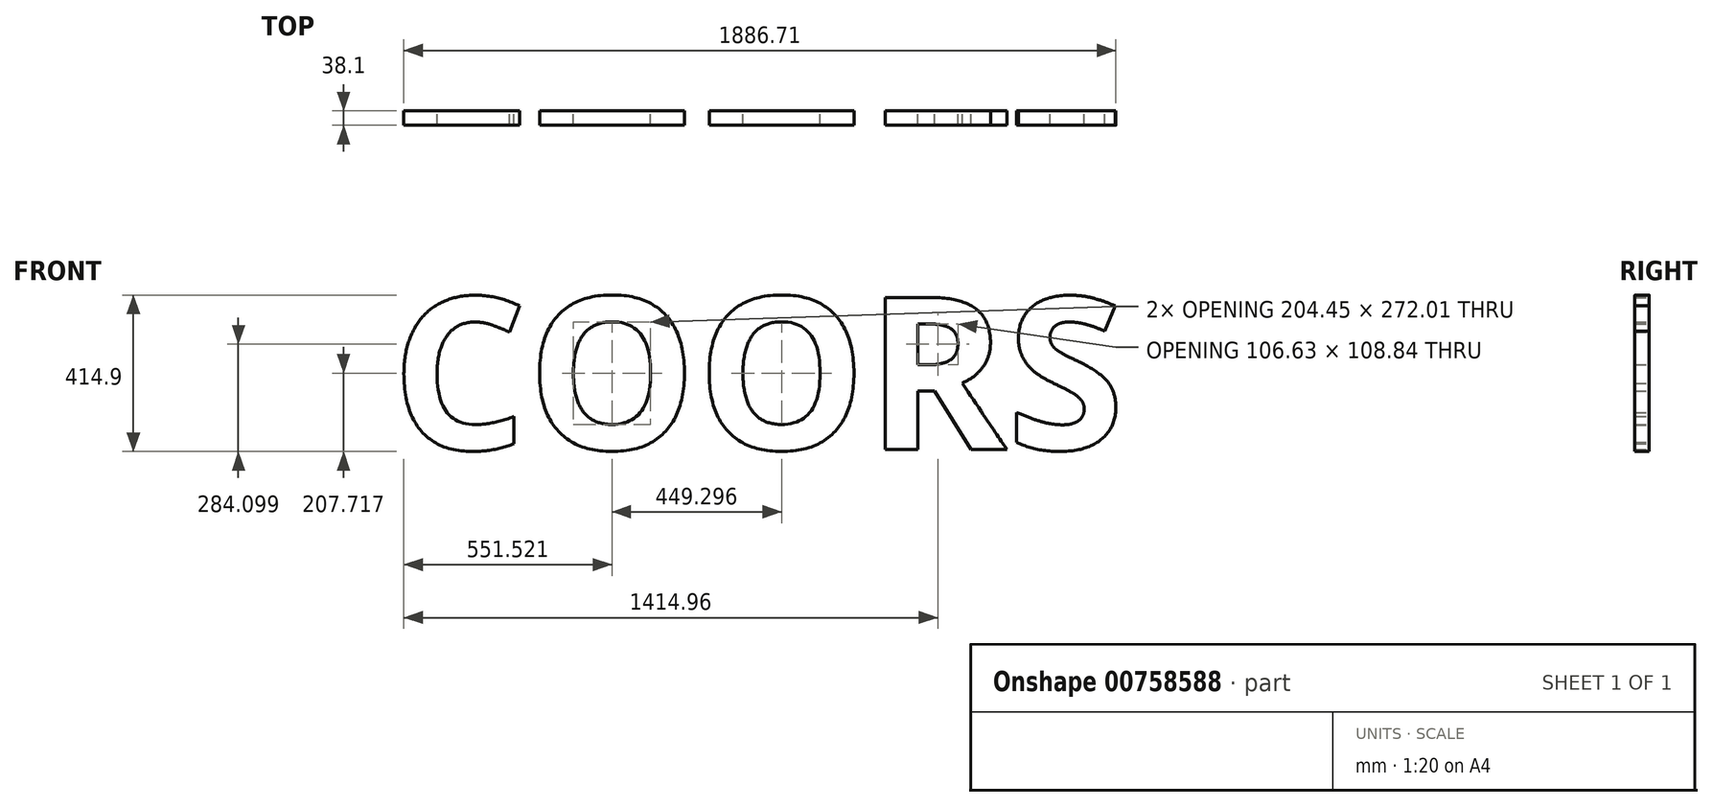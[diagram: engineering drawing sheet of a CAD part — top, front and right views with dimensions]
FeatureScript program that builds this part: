
annotation { "Feature Type Name" : "Feature", "Feature Type Description" : "" }
export const myFeature = defineFeature(function(context is Context, id is Id, definition is map)
    precondition{}
    {
        {
            var Q0;
            Q0=qCreatedBy(makeId("Front.planeOp"),FACE);
            var sketch = newSketch(context, id + "F0", { "sketchPlane" : qUnion([Q0])});
            skLineSegment(sketch, "E0.bottom", {"start": v(-1016, 228.6) * mm, "end": v(1016, 228.6) * mm});
            skLineSegment(sketch, "E0.top", {"start": v(-1016, -228.6) * mm, "end": v(1016, -228.6) * mm});
            skLineSegment(sketch, "E0.left", {"start": v(-1016, 228.6) * mm, "end": v(-1016, -228.6) * mm});
            skLineSegment(sketch, "E0.right", {"start": v(1016, 228.6) * mm, "end": v(1016, -228.6) * mm});
            skPoint(sketch, "E0.middle", {"position": v(0, 0) * mm});
            skText(sketch, "E1", { "text": "COORS", "fontName": "OpenSans-Bold.ttf"});
            const initialGuessF0  = {"E1": [-0.98102, -0.20588, 1, 0, 0.40643]};
            skSetInitialGuess(sketch, initialGuessF0);
            skSolve(sketch);
        }
        {
            var Q0;
            Q0=makeQuery(id+"F0.imprint","IMPRINT",FACE,{"disambiguationData":[TD([[makeQuery(id+"F0.imprint","IMPRINT",EDGE,{"derivedFrom":sQuery(id+"F0.wireOp",EDGE,"E1.sketch_text.stroke-0")}),-1.0]])]});
            extrude(context, id + "F1", {"entities" : qUnion([Q0]), "depth" : 38.1 * mm, "offsetDistance" : 25.4 * mm});
        }
        {
            var Q0;
            Q0=makeQuery(id+"F0.imprint","IMPRINT",FACE,{"disambiguationData":[TD([[makeQuery(id+"F0.imprint","IMPRINT",EDGE,{"derivedFrom":sQuery(id+"F0.wireOp",EDGE,"E1.sketch_text.stroke-15")}),-1.0]])]});
            extrude(context, id + "F2", {"entities" : qUnion([Q0]), "depth" : 38.1 * mm, "offsetDistance" : 25.4 * mm});
        }
        {
            var Q0;
            Q0=makeQuery(id+"F0.imprint","IMPRINT",FACE,{"disambiguationData":[TD([[makeQuery(id+"F0.imprint","IMPRINT",EDGE,{"derivedFrom":sQuery(id+"F0.wireOp",EDGE,"E1.sketch_text.stroke-29")}),-1.0]])]});
            var Q1;
            Q1=makeQuery(id+"F0.imprint","IMPRINT",FACE,{"disambiguationData":[TD([[makeQuery(id+"F0.imprint","IMPRINT",EDGE,{"derivedFrom":sQuery(id+"F0.wireOp",EDGE,"E1.sketch_text.stroke-43")}),-1.0]])]});
            var Q2;
            Q2=makeQuery(id+"F0.imprint","IMPRINT",FACE,{"disambiguationData":[TD([[makeQuery(id+"F0.imprint","IMPRINT",EDGE,{"derivedFrom":sQuery(id+"F0.wireOp",EDGE,"E1.sketch_text.stroke-62")}),-1.0]])]});
            extrude(context, id + "F3", {"entities" : qUnion([Q0, Q1, Q2]), "depth" : 38.1 * mm, "offsetDistance" : 25.4 * mm});
        }
    });
